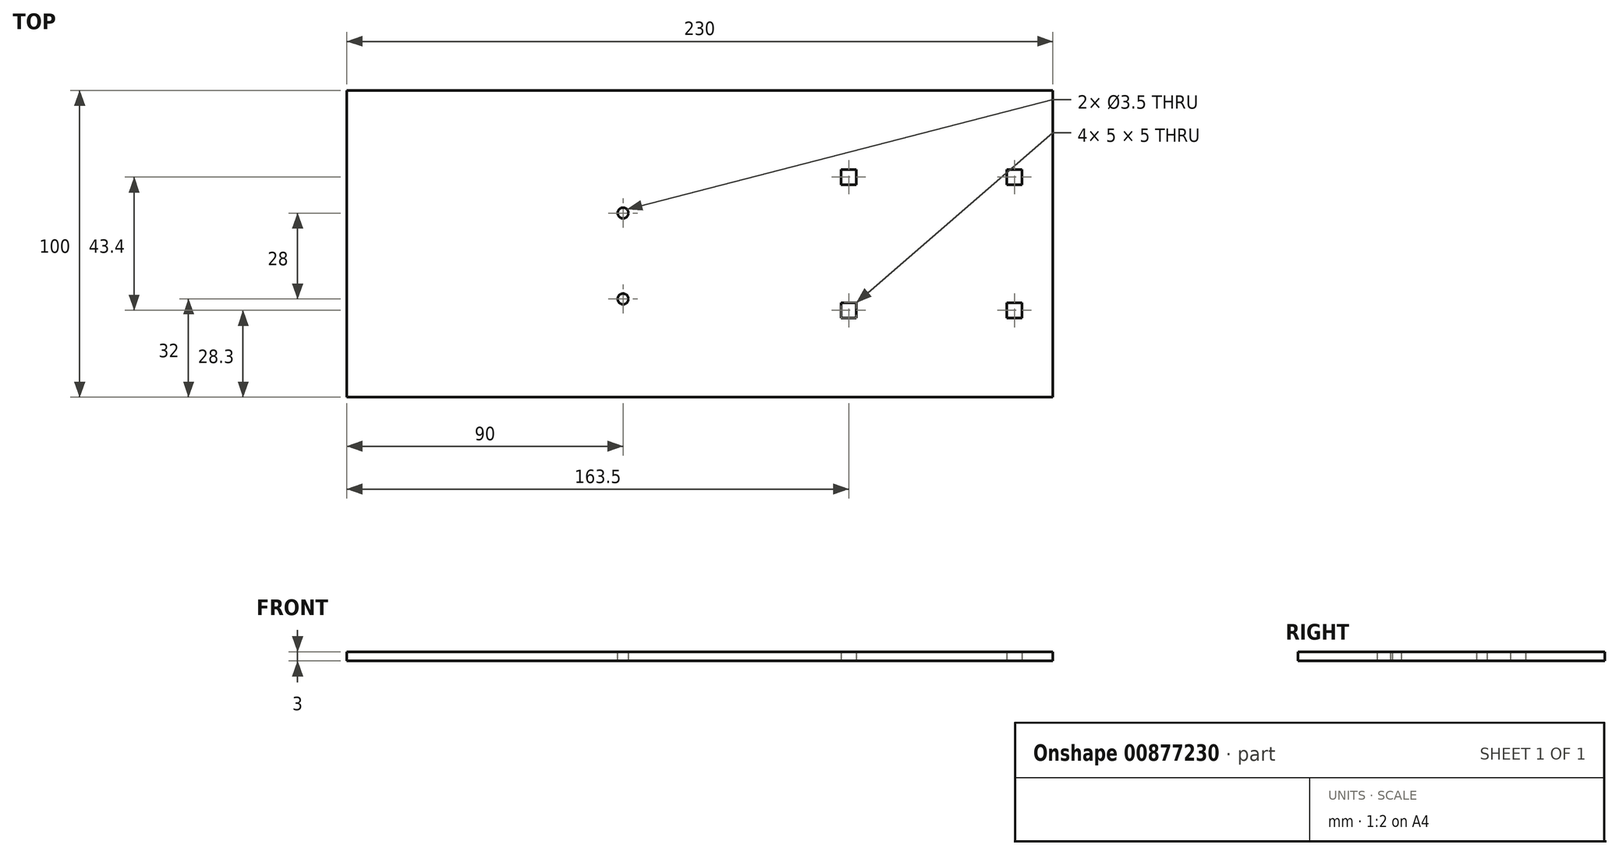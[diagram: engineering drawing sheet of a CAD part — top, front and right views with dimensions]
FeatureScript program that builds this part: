
annotation { "Feature Type Name" : "Feature", "Feature Type Description" : "" }
export const myFeature = defineFeature(function(context is Context, id is Id, definition is map)
    precondition{}
    {
        {
            var Q0;
            Q0=qCreatedBy(makeId("Top.planeOp"),FACE);
            var sketch = newSketch(context, id + "F0", { "sketchPlane" : qUnion([Q0])});
            skLineSegment(sketch, "E0.bottom", {"start": v(-180, 50) * mm, "end": v(50, 50) * mm});
            skLineSegment(sketch, "E0.top", {"start": v(-180, -50) * mm, "end": v(50, -50) * mm});
            skLineSegment(sketch, "E0.left", {"start": v(-180, 50) * mm, "end": v(-180, -50) * mm});
            skLineSegment(sketch, "E0.right", {"start": v(50, 50) * mm, "end": v(50, -50) * mm});
            skLineSegment(sketch, "E1.bottom", {"start": v(-19, 24.2) * mm, "end": v(-14, 24.2) * mm});
            skLineSegment(sketch, "E1.top", {"start": v(-19, 19.2) * mm, "end": v(-14, 19.2) * mm});
            skLineSegment(sketch, "E1.left", {"start": v(-19, 24.2) * mm, "end": v(-19, 19.2) * mm});
            skLineSegment(sketch, "E1.right", {"start": v(-14, 24.2) * mm, "end": v(-14, 19.2) * mm});
            skLineSegment(sketch, "E2.3.0.0", {"start": v(35, 19.2) * mm, "end": v(40, 19.2) * mm});
            skLineSegment(sketch, "E2.3.0.1", {"start": v(40, 24.2) * mm, "end": v(40, 19.2) * mm});
            skLineSegment(sketch, "E2.3.0.2", {"start": v(35, 24.2) * mm, "end": v(35, 19.2) * mm});
            skLineSegment(sketch, "E2.3.0.3", {"start": v(35, 24.2) * mm, "end": v(40, 24.2) * mm});
            skLineSegment(sketch, "E3.MirrorCS", {"start": v(40, -24.2) * mm, "end": v(40, -19.2) * mm});
            skLineSegment(sketch, "E4.MirrorCS", {"start": v(-19, -19.2) * mm, "end": v(-14, -19.2) * mm});
            skLineSegment(sketch, "E5.MirrorCS", {"start": v(35, -19.2) * mm, "end": v(40, -19.2) * mm});
            skLineSegment(sketch, "E6.MirrorCS", {"start": v(-14, -24.2) * mm, "end": v(-14, -19.2) * mm});
            skLineSegment(sketch, "E7.MirrorCS", {"start": v(-19, -24.2) * mm, "end": v(-14, -24.2) * mm});
            skLineSegment(sketch, "E8.MirrorCS", {"start": v(-19, -24.2) * mm, "end": v(-19, -19.2) * mm});
            skLineSegment(sketch, "E9.MirrorCS", {"start": v(35, -24.2) * mm, "end": v(40, -24.2) * mm});
            skLineSegment(sketch, "E10.MirrorCS", {"start": v(35, -24.2) * mm, "end": v(35, -19.2) * mm});
            skSolve(sketch);
        }
        {
            var Q0;
            Q0=makeQuery(id+"F0.imprint","IMPRINT",FACE,{"disambiguationData":[TD([[makeQuery(id+"F0.imprint","IMPRINT",EDGE,{"derivedFrom":sQuery(id+"F0.wireOp",EDGE,"E0.bottom")}),-1.0]])]});
            extrude(context, id + "F1", {"entities" : qUnion([Q0]), "depth" : 3 * mm, "offsetDistance" : 25 * mm});
        }
        {
            var Q0;
            Q0=makeQuery(id+"F1.opExtrude","CAP_FACE",FACE,{"disambiguationData":[OSD([sQuery(id+"F0.wireOp",EDGE,"E0.bottom"),sQuery(id+"F0.wireOp",EDGE,"E0.top"),sQuery(id+"F0.wireOp",EDGE,"E0.left"),sQuery(id+"F0.wireOp",EDGE,"E0.right"),sQuery(id+"F0.wireOp",EDGE,"E1.bottom"),sQuery(id+"F0.wireOp",EDGE,"E1.top"),sQuery(id+"F0.wireOp",EDGE,"E1.left"),sQuery(id+"F0.wireOp",EDGE,"E1.right"),sQuery(id+"F0.wireOp",EDGE,"E2.3.0.0"),sQuery(id+"F0.wireOp",EDGE,"E2.3.0.1"),sQuery(id+"F0.wireOp",EDGE,"E2.3.0.2"),sQuery(id+"F0.wireOp",EDGE,"E2.3.0.3"),sQuery(id+"F0.wireOp",EDGE,"E3.MirrorCS"),sQuery(id+"F0.wireOp",EDGE,"E4.MirrorCS"),sQuery(id+"F0.wireOp",EDGE,"E5.MirrorCS"),sQuery(id+"F0.wireOp",EDGE,"E6.MirrorCS"),sQuery(id+"F0.wireOp",EDGE,"E7.MirrorCS"),sQuery(id+"F0.wireOp",EDGE,"E8.MirrorCS"),sQuery(id+"F0.wireOp",EDGE,"E9.MirrorCS"),sQuery(id+"F0.wireOp",EDGE,"E10.MirrorCS")])],"isStart":false});
            var sketch = newSketch(context, id + "F2", { "sketchPlane" : qUnion([Q0])});
            skLineSegment(sketch, "E11.bottom", {"start": v(-59.96, 0) * mm, "end": v(57.84, 0) * mm});
            skLineSegment(sketch, "E11.top", {"start": v(-59.96, -58.9) * mm, "end": v(57.84, -58.9) * mm});
            skLineSegment(sketch, "E11.left", {"start": v(-59.96, 0) * mm, "end": v(-59.96, -58.9) * mm});
            skLineSegment(sketch, "E11.right", {"start": v(57.84, 0) * mm, "end": v(57.84, -58.9) * mm});
            skSolve(sketch);
        }
        {
            var Q0;
            {var subQ7=makeQuery(id+"F1.opExtrude","CAP_EDGE",EDGE,{"disambiguationData":[OSD([sQuery(id+"F0.wireOp",EDGE,"E0.bottom")])],"isStart":false});Q0=makeQuery(id+"F2.imprint","IMPRINT",FACE,{"disambiguationData":[TD([[makeQuery(id+"F2.imprint","IMPRINT",EDGE,{"derivedFrom":subQ7}),-1.0]])]});}
            var sketch = newSketch(context, id + "F3", { "sketchPlane" : qUnion([Q0])});
            skCircle(sketch, "E12", {"center": v(-90, 10) * mm, "radius": 1.75 * mm});
            skCircle(sketch, "E13", {"center": v(-90, -18) * mm, "radius": 1.75 * mm});
            skSolve(sketch);
        }
        {
            var Q0;
            Q0 = qSketchRegion(id + "F3", true);
            extrude(context, id + "F4", {"entities" : qUnion([Q0]), "operationType" : NewBodyOperationType.REMOVE, "oppositeDirection" : true, "depth" : 25 * mm, "offsetDistance" : 25 * mm});
        }
    });
